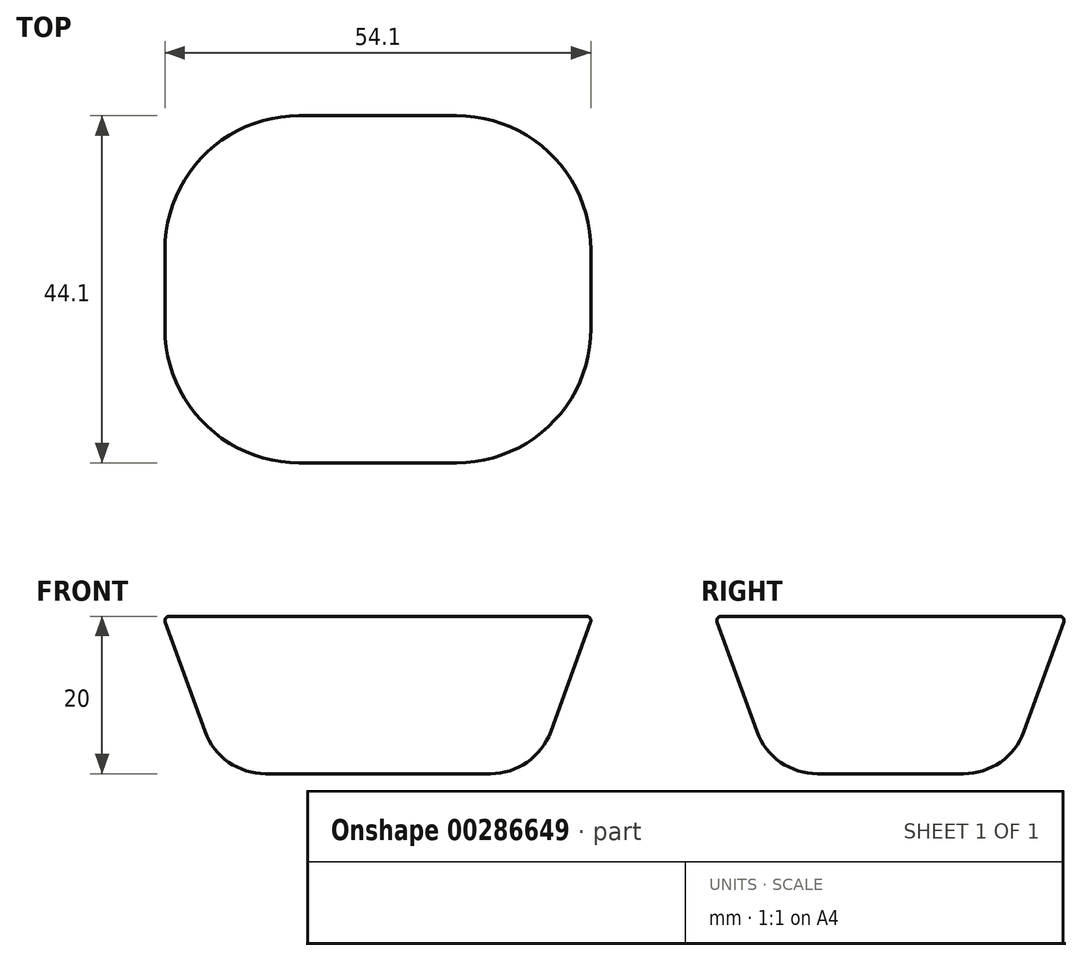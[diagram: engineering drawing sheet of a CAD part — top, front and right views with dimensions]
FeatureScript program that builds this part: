
annotation { "Feature Type Name" : "Feature", "Feature Type Description" : "" }
export const myFeature = defineFeature(function(context is Context, id is Id, definition is map)
    precondition{}
    {
        {
            var Q0;
            Q0=qCreatedBy(makeId("Top.planeOp"),FACE);
            var sketch = newSketch(context, id + "F0", { "sketchPlane" : qUnion([Q0])});
            skLineSegment(sketch, "E0.bottom", {"start": v(-5.53, 17.03) * mm, "end": v(14.47, 17.03) * mm});
            skLineSegment(sketch, "E0.top", {"start": v(-5.53, -12.97) * mm, "end": v(14.47, -12.97) * mm});
            skLineSegment(sketch, "E0.left", {"start": v(-15.53, 7.03) * mm, "end": v(-15.53, -2.97) * mm});
            skLineSegment(sketch, "E0.right", {"start": v(24.47, 7.03) * mm, "end": v(24.47, -2.97) * mm});
            skPoint(sketch, "E1.visualSharp", {"position": v(-15.53, -12.97) * mm});
            skArc(sketch, "E1.filletArc", {"start": v(-15.53, -2.97) * mm, "mid": v(-12.6, -10.04) * mm, "end": v(-5.53, -12.97) * mm});
            skPoint(sketch, "E2.visualSharp", {"position": v(-15.53, 17.03) * mm});
            skArc(sketch, "E2.filletArc", {"start": v(-5.53, 17.03) * mm, "mid": v(-12.6, 14.1) * mm, "end": v(-15.53, 7.03) * mm});
            skPoint(sketch, "E3.visualSharp", {"position": v(24.47, 17.03) * mm});
            skArc(sketch, "E3.filletArc", {"start": v(24.47, 7.03) * mm, "mid": v(21.54, 14.1) * mm, "end": v(14.47, 17.03) * mm});
            skPoint(sketch, "E4.visualSharp", {"position": v(24.47, -12.97) * mm});
            skArc(sketch, "E4.filletArc", {"start": v(14.47, -12.97) * mm, "mid": v(21.54, -10.04) * mm, "end": v(24.47, -2.97) * mm});
            skSolve(sketch);
        }
        {
            var Q0;
            Q0=makeQuery(id+"F0.imprint","IMPRINT",FACE,{"disambiguationData":[TD([[makeQuery(id+"F0.imprint","IMPRINT",EDGE,{"derivedFrom":sQuery(id+"F0.wireOp",EDGE,"E0.bottom")}),-1.0]])]});
            extrude(context, id + "F1", {"entities" : qUnion([Q0]), "depth" : 20 * mm, "hasDraft" : true, "draftAngle" : 20 * degree});
        }
        {
            var Q0;
            Q0=makeQuery(id+"F1.opExtrude","CAP_FACE",FACE,{"disambiguationData":[OSD([sQuery(id+"F0.wireOp",EDGE,"E0.bottom"),sQuery(id+"F0.wireOp",EDGE,"E0.top"),sQuery(id+"F0.wireOp",EDGE,"E0.left"),sQuery(id+"F0.wireOp",EDGE,"E0.right"),sQuery(id+"F0.wireOp",EDGE,"E1.filletArc"),sQuery(id+"F0.wireOp",EDGE,"E2.filletArc"),sQuery(id+"F0.wireOp",EDGE,"E3.filletArc"),sQuery(id+"F0.wireOp",EDGE,"E4.filletArc")])],"isStart":true});
            fillet(context, id + "F2", {"entities" : qUnion([Q0]), "radius" : 8.15 * mm, "tangentPropagation" : true, "allowEdgeOverflow" : false});
        }
        {
            var Q0;
            Q0=makeQuery(id+"F1.opExtrude","CAP_FACE",FACE,{"disambiguationData":[OSD([sQuery(id+"F0.wireOp",EDGE,"E0.bottom"),sQuery(id+"F0.wireOp",EDGE,"E0.top"),sQuery(id+"F0.wireOp",EDGE,"E0.left"),sQuery(id+"F0.wireOp",EDGE,"E0.right"),sQuery(id+"F0.wireOp",EDGE,"E1.filletArc"),sQuery(id+"F0.wireOp",EDGE,"E2.filletArc"),sQuery(id+"F0.wireOp",EDGE,"E3.filletArc"),sQuery(id+"F0.wireOp",EDGE,"E4.filletArc")])],"isStart":false});
            fillet(context, id + "F3", {"entities" : qUnion([Q0]), "radius" : 0.54 * mm, "tangentPropagation" : true, "allowEdgeOverflow" : false});
        }
    });
